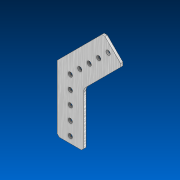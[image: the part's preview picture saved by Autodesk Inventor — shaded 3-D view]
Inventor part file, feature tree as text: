
AUTODESK INVENTOR PART (.ipt)
format: ipt  version: 2022.2 (Build 262287000, 287)  size: 113,152 bytes
history: native  units: in
note: dims shown in document units (in); Inventor stores cm internally (conversion verified against a paired STEP export)
features: fillet x1
ambient origin geometry x8: Origin, YZ Plane, XZ Plane, XY Plane, X Axis, Y Axis, Z Axis, Center Point
bodies: Solid1 (feature_tree)
feature tree (1):
  fillet  "Fillet2"  [1 undecoded]
note: 1 required parameter value undecoded (feature->parameter linkage not recoverable at this tier; creation-order binding heuristic only, values carry confidence <= 0.55)
